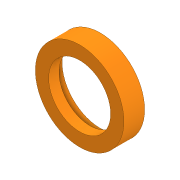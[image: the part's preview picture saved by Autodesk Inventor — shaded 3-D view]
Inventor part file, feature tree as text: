
AUTODESK INVENTOR PART (.ipt)
format: ipt  version: 2020 (Build 240168000, 168)  size: 96,768 bytes
history: native  units: in
note: dims shown in document units (in); Inventor stores cm internally (conversion verified against a paired STEP export)
features: extrude x2, sketch x2
ambient origin geometry x8: Origin, YZ Plane, XZ Plane, XY Plane, X Axis, Y Axis, Z Axis, Center Point
bodies: Solid1 (feature_tree)
feature tree (4):
  extrude  "Extrusion1"  Depth=2.0472in
  extrude  "Extrusion2"  Depth=0.2756in
  sketch  "Sketch1"  dims[d0=2.3622in d1=2.0472in]
  sketch  "Sketch2"  dims[d2=0.2756in d3=0.0in d4=1.6535in d5=0.2756in d6=0.0in]
